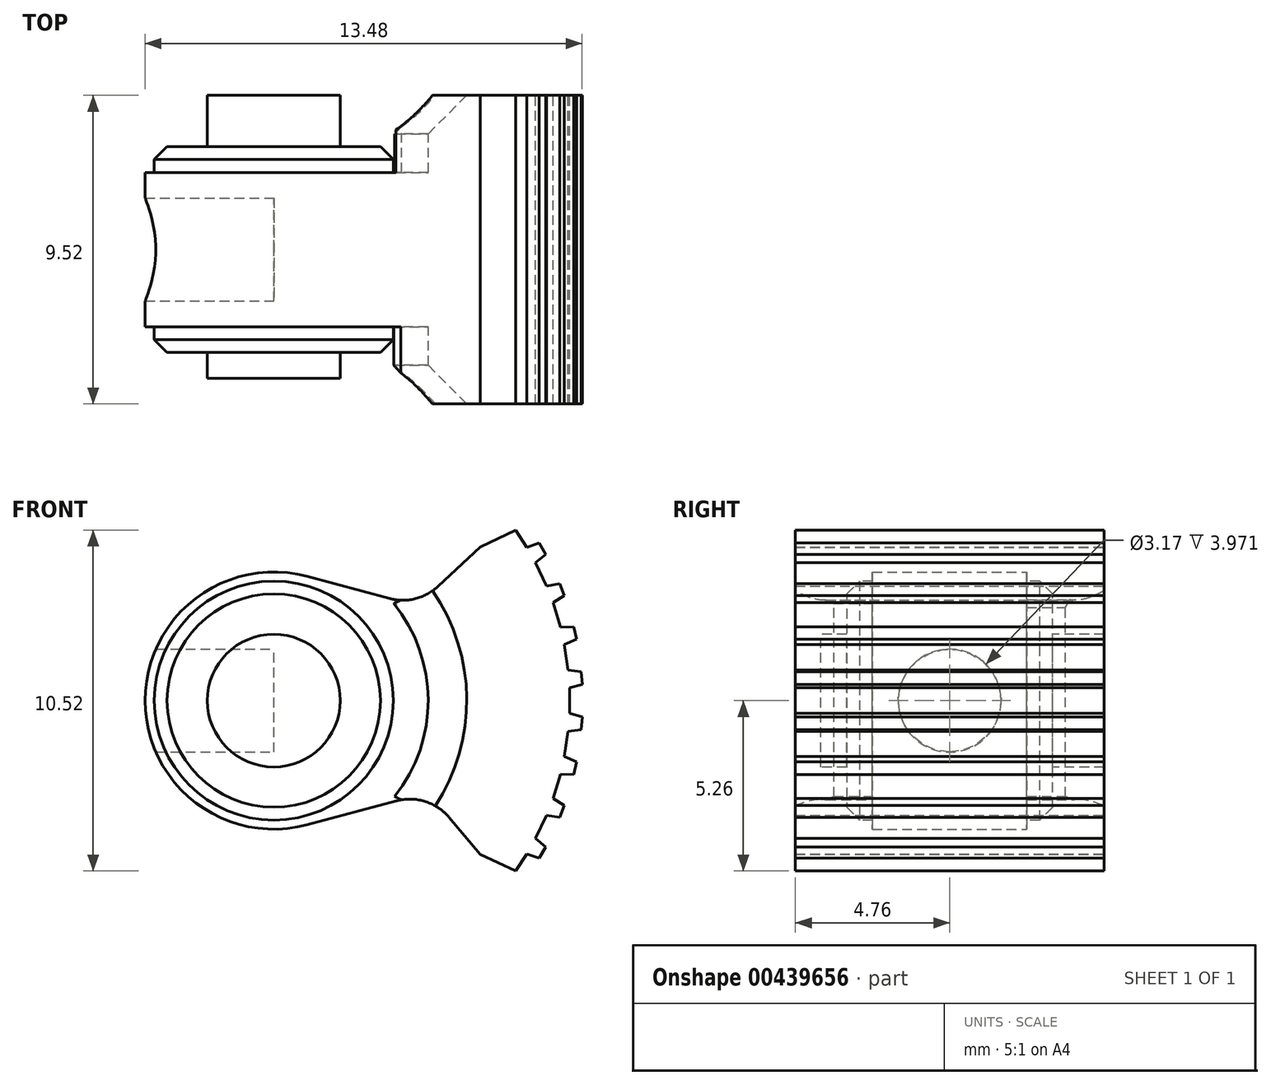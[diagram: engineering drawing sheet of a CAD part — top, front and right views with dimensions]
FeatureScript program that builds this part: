
annotation { "Feature Type Name" : "Feature", "Feature Type Description" : "" }
export const myFeature = defineFeature(function(context is Context, id is Id, definition is map)
    precondition{}
    {
        {
            var Q0;
            Q0=qCreatedBy(makeId("Front.planeOp"),FACE);
            var sketch = newSketch(context, id + "F0", { "sketchPlane" : qUnion([Q0])});
            skCircle(sketch, "E0", {"center": v(0, 0) * mm, "radius": 9.53 * mm, "construction": true});
            skCircle(sketch, "E1", {"center": v(0, 0) * mm, "radius": 7.94 * mm, "construction": true});
            skCircle(sketch, "E2", {"center": v(0, 0) * mm, "radius": 4.76 * mm, "construction": true});
            skCircle(sketch, "E3", {"center": v(0, 0) * mm, "radius": 3.97 * mm});
            skLineSegment(sketch, "E4", {"start": v(-17.92, 8.9) * mm, "end": v(15.33, 0) * mm, "construction": true});
            skLineSegment(sketch, "E5", {"start": v(-17.92, -8.9) * mm, "end": v(15.33, 0) * mm, "construction": true});
            skLineSegment(sketch, "E6", {"start": v(3.57, 3.15) * mm, "end": v(1.03, 3.83) * mm});
            skLineSegment(sketch, "E7", {"start": v(3.78, -3.1) * mm, "end": v(1.03, -3.83) * mm});
            skArc(sketch, "E8", {"start": v(4.23, -2.2) * mm, "mid": v(4.76, 0) * mm, "end": v(4.23, 2.2) * mm});
            skLineSegment(sketch, "E9", {"start": v(2.38, 0) * mm, "end": v(14.12, 14) * mm, "construction": true});
            skLineSegment(sketch, "E10", {"start": v(2.38, 0) * mm, "end": v(14.12, -14) * mm, "construction": true});
            skLineSegment(sketch, "E11", {"start": v(5.07, 3.53) * mm, "end": v(6.36, 4.75) * mm});
            skLineSegment(sketch, "E12", {"start": v(5.4, -3.6) * mm, "end": v(6.36, -4.75) * mm});
            skArc(sketch, "E13.filletArc", {"start": v(3.57, 3.15) * mm, "mid": v(4.37, 3.15) * mm, "end": v(5.07, 3.53) * mm});
            skArc(sketch, "E14.filletArc", {"start": v(5.4, -3.6) * mm, "mid": v(4.67, -3.11) * mm, "end": v(3.78, -3.1) * mm});
            skLineSegment(sketch, "E15", {"start": v(6.36, 4.75) * mm, "end": v(14.46, 8.52) * mm, "construction": true});
            skLineSegment(sketch, "E16", {"start": v(6.36, -4.75) * mm, "end": v(14.46, -8.52) * mm, "construction": true});
            skLineSegment(sketch, "E17", {"start": v(6.36, 4.75) * mm, "end": v(7.83, 5.43) * mm});
            skLineSegment(sketch, "E18", {"start": v(6.36, -4.75) * mm, "end": v(7.83, -5.43) * mm});
            skArc(sketch, "E19", {"start": v(7.83, -5.43) * mm, "mid": v(9.53, 0) * mm, "end": v(7.83, 5.43) * mm});
            skCircle(sketch, "E20", {"center": v(0, 0) * mm, "radius": 9.13 * mm, "construction": true});
            skSolve(sketch);
        }
        {
            var Q0;
            Q0=qSketchRegion(id+"F0",true);
            extrude(context, id + "F1", {"entities" : qUnion([Q0]), "endBound" : BoundingType.SYMMETRIC, "depth" : 4.76 * mm});
        }
        {
            var Q0;
            Q0=qCreatedBy(makeId("Top.planeOp"),FACE);
            var sketch = newSketch(context, id + "F2", { "sketchPlane" : qUnion([Q0])});
            skLineSegment(sketch, "E21", {"start": v(0, -3.18) * mm, "end": v(0, 3.18) * mm});
            skLineSegment(sketch, "E22", {"start": v(0, 3.18) * mm, "end": v(0, 4.76) * mm});
            skLineSegment(sketch, "E23", {"start": v(0, 4.76) * mm, "end": v(2.05, 4.76) * mm});
            skLineSegment(sketch, "E24", {"start": v(2.05, 4.76) * mm, "end": v(2.05, 3.18) * mm});
            skLineSegment(sketch, "E25", {"start": v(2.05, 3.18) * mm, "end": v(3.69, 3.18) * mm});
            skLineSegment(sketch, "E26", {"start": v(3.69, 3.18) * mm, "end": v(3.69, -3.18) * mm});
            skLineSegment(sketch, "E27", {"start": v(3.69, -3.18) * mm, "end": v(2.05, -3.18) * mm});
            skLineSegment(sketch, "E28", {"start": v(2.05, -3.18) * mm, "end": v(2.05, -3.97) * mm});
            skLineSegment(sketch, "E29", {"start": v(2.05, -3.97) * mm, "end": v(0, -3.97) * mm});
            skLineSegment(sketch, "E30", {"start": v(0, -3.97) * mm, "end": v(0, -3.18) * mm});
            skSolve(sketch);
        }
        {
            var Q0;
            Q0=makeQuery(id+"F2.imprint","IMPRINT",FACE,{"disambiguationData":[TD([[makeQuery(id+"F2.imprint","IMPRINT",EDGE,{"derivedFrom":sQuery(id+"F2.wireOp",EDGE,"E21")}),-1.0]])]});
            var Q1;
            Q1=sQuery(id+"F2.wireOp",EDGE,"E21");
            revolve(context, id + "F3", {"operationType" : NewBodyOperationType.ADD, "entities" : qUnion([Q0]), "axis" : qUnion([Q1]), "revolveType" : RevolveType.FULL});
        }
        {
            var Q0;
            Q0=qCreatedBy(makeId("Front.planeOp"),FACE);
            var sketch = newSketch(context, id + "F4", { "sketchPlane" : qUnion([Q0])});
            skArc(sketch, "E31.0", {"start": v(7.83, -5.43) * mm, "mid": v(9.53, 0) * mm, "end": v(7.83, 5.43) * mm});
            skLineSegment(sketch, "E32.0", {"start": v(6.36, 4.75) * mm, "end": v(7.83, 5.43) * mm});
            skLineSegment(sketch, "E33.0", {"start": v(5.07, 3.53) * mm, "end": v(6.36, 4.75) * mm});
            skLineSegment(sketch, "E33.1", {"start": v(5.4, -3.6) * mm, "end": v(6.36, -4.75) * mm});
            skLineSegment(sketch, "E33.2", {"start": v(6.36, -4.75) * mm, "end": v(7.83, -5.43) * mm});
            skArc(sketch, "E34.0", {"start": v(3.57, 3.15) * mm, "mid": v(4.37, 3.15) * mm, "end": v(5.07, 3.53) * mm});
            skArc(sketch, "E34.1", {"start": v(5.4, -3.6) * mm, "mid": v(4.67, -3.11) * mm, "end": v(3.78, -3.1) * mm});
            skCircle(sketch, "E35", {"center": v(0, 0) * mm, "radius": 4.76 * mm, "construction": true});
            skLineSegment(sketch, "E36.0", {"start": v(3.57, 3.15) * mm, "end": v(3.57, 3.15) * mm});
            skLineSegment(sketch, "E37.0", {"start": v(3.78, -3.1) * mm, "end": v(3.57, -3.15) * mm});
            skArc(sketch, "E38", {"start": v(3.57, -3.15) * mm, "mid": v(4.76, 0) * mm, "end": v(3.57, 3.15) * mm});
            skPoint(sketch, "E39.orphan", {"position": v(1.03, 3.83) * mm});
            skPoint(sketch, "E40.orphan", {"position": v(1.03, -3.83) * mm});
            skSolve(sketch);
        }
        {
            var Q0;
            Q0=qSketchRegion(id+"F4",true);
            extrude(context, id + "F5", {"entities" : qUnion([Q0]), "operationType" : NewBodyOperationType.ADD, "endBound" : BoundingType.SYMMETRIC, "depth" : 9.52 * mm});
        }
        {
            var Q0;
            Q0=makeQuery(id+"F3.opRevolve","SWEPT_EDGE",EDGE,{"disambiguationData":[OSD([sQuery(id+"F2.wireOp",EDGE,"E26"),sQuery(id+"F2.wireOp",EDGE,"E27")])]});
            var Q1;
            Q1=makeQuery(id+"F3.opRevolve","SWEPT_EDGE",EDGE,{"disambiguationData":[OSD([sQuery(id+"F2.wireOp",EDGE,"E25"),sQuery(id+"F2.wireOp",EDGE,"E26")])]});
            chamfer(context, id + "F6", {"entities" : qUnion([Q0, Q1]), "chamferType" : ChamferType.OFFSET_ANGLE, "width" : 0.4 * mm, "oppositeDirection" : false, "angle" : 45 * degree, "tangentPropagation" : true});
        }
        {
            var Q0;
            Q0=makeQuery(id+"F5.opExtrude","CAP_EDGE",EDGE,{"disambiguationData":[OSD([sQuery(id+"F4.wireOp",EDGE,"E38")])],"isStart":false});
            var Q1;
            Q1=makeQuery(id+"F5.opExtrude","CAP_EDGE",EDGE,{"disambiguationData":[OSD([sQuery(id+"F4.wireOp",EDGE,"E38")])],"isStart":true});
            chamfer(context, id + "F7", {"entities" : qUnion([Q0, Q1]), "chamferType" : ChamferType.OFFSET_ANGLE, "width" : 1.2 * mm, "oppositeDirection" : false, "angle" : 45 * degree, "tangentPropagation" : true});
        }
        {
            var Q0;
            {var subQ0=sQuery(id+"F4.wireOp",EDGE,"E37.0");var subQ2=sQuery(id+"F4.wireOp",EDGE,"E38");Q0=makeQuery(id+"F5.boolean.opBoolean","SPLIT",EDGE,{"disambiguationData":[TD([makeQuery(id+"F5.opExtrude","CAP_FACE",FACE,{"disambiguationData":[OSD([sQuery(id+"F4.wireOp",EDGE,"E31.0"),sQuery(id+"F4.wireOp",EDGE,"E32.0"),sQuery(id+"F4.wireOp",EDGE,"E33.0"),sQuery(id+"F4.wireOp",EDGE,"E33.1"),sQuery(id+"F4.wireOp",EDGE,"E33.2"),sQuery(id+"F4.wireOp",EDGE,"E34.0"),sQuery(id+"F4.wireOp",EDGE,"E34.1"),subQ0,subQ2])],"isStart":false})])],"derivedFrom":makeQuery(id+"F5.opExtrude","SWEPT_EDGE",EDGE,{"disambiguationData":[OSD([subQ0,subQ2])]})});}
            var Q1;
            {var subQ0=sQuery(id+"F4.wireOp",EDGE,"E37.0");var subQ1=sQuery(id+"F4.wireOp",EDGE,"E38");Q1=makeQuery(id+"F5.boolean.opBoolean","SPLIT",EDGE,{"disambiguationData":[TD([makeQuery(id+"F5.opExtrude","CAP_FACE",FACE,{"disambiguationData":[OSD([sQuery(id+"F4.wireOp",EDGE,"E31.0"),sQuery(id+"F4.wireOp",EDGE,"E32.0"),sQuery(id+"F4.wireOp",EDGE,"E33.0"),sQuery(id+"F4.wireOp",EDGE,"E33.1"),sQuery(id+"F4.wireOp",EDGE,"E33.2"),sQuery(id+"F4.wireOp",EDGE,"E34.0"),sQuery(id+"F4.wireOp",EDGE,"E34.1"),subQ0,subQ1])],"isStart":true})])],"derivedFrom":makeQuery(id+"F5.opExtrude","SWEPT_EDGE",EDGE,{"disambiguationData":[OSD([subQ0,subQ1])]})});}
            var Q2;
            {var subQ1=sQuery(id+"F4.wireOp",EDGE,"E38");var subQ2=sQuery(id+"F4.wireOp",EDGE,"E34.0");Q2=makeQuery(id+"F5.boolean.opBoolean","SPLIT",EDGE,{"disambiguationData":[TD([makeQuery(id+"F5.opExtrude","CAP_FACE",FACE,{"disambiguationData":[OSD([sQuery(id+"F4.wireOp",EDGE,"E31.0"),sQuery(id+"F4.wireOp",EDGE,"E32.0"),sQuery(id+"F4.wireOp",EDGE,"E33.0"),sQuery(id+"F4.wireOp",EDGE,"E33.1"),sQuery(id+"F4.wireOp",EDGE,"E33.2"),subQ2,sQuery(id+"F4.wireOp",EDGE,"E34.1"),sQuery(id+"F4.wireOp",EDGE,"E37.0"),subQ1])],"isStart":false})])],"derivedFrom":makeQuery(id+"F5.opExtrude","SWEPT_EDGE",EDGE,{"disambiguationData":[OSD([subQ2,subQ1])]})});}
            var Q3;
            {var subQ0=sQuery(id+"F4.wireOp",EDGE,"E38");var subQ1=sQuery(id+"F4.wireOp",EDGE,"E34.0");Q3=makeQuery(id+"F5.boolean.opBoolean","SPLIT",EDGE,{"disambiguationData":[TD([makeQuery(id+"F5.opExtrude","CAP_FACE",FACE,{"disambiguationData":[OSD([sQuery(id+"F4.wireOp",EDGE,"E31.0"),sQuery(id+"F4.wireOp",EDGE,"E32.0"),sQuery(id+"F4.wireOp",EDGE,"E33.0"),sQuery(id+"F4.wireOp",EDGE,"E33.1"),sQuery(id+"F4.wireOp",EDGE,"E33.2"),subQ1,sQuery(id+"F4.wireOp",EDGE,"E34.1"),sQuery(id+"F4.wireOp",EDGE,"E37.0"),subQ0])],"isStart":true})])],"derivedFrom":makeQuery(id+"F5.opExtrude","SWEPT_EDGE",EDGE,{"disambiguationData":[OSD([subQ1,subQ0])]})});}
            chamfer(context, id + "F8", {"entities" : qUnion([Q0, Q1, Q2, Q3]), "chamferType" : ChamferType.OFFSET_ANGLE, "width" : 0.4 * mm, "oppositeDirection" : false, "angle" : 45 * degree, "tangentPropagation" : true});
        }
        {
            var Q0;
            Q0=makeQuery(id+"F5.opExtrude","CAP_FACE",FACE,{"disambiguationData":[OSD([sQuery(id+"F4.wireOp",EDGE,"E31.0"),sQuery(id+"F4.wireOp",EDGE,"E32.0"),sQuery(id+"F4.wireOp",EDGE,"E33.0"),sQuery(id+"F4.wireOp",EDGE,"E33.1"),sQuery(id+"F4.wireOp",EDGE,"E33.2"),sQuery(id+"F4.wireOp",EDGE,"E34.0"),sQuery(id+"F4.wireOp",EDGE,"E34.1"),sQuery(id+"F4.wireOp",EDGE,"E37.0"),sQuery(id+"F4.wireOp",EDGE,"E38")])],"isStart":true});
            var sketch = newSketch(context, id + "F9", { "sketchPlane" : qUnion([Q0])});
            skArc(sketch, "E41.0", {"start": v(-7.83, -5.43) * mm, "mid": v(-9.53, 0) * mm, "end": v(-7.83, 5.43) * mm, "construction": true});
            skCircle(sketch, "E42", {"center": v(0, 0) * mm, "radius": 9.13 * mm, "construction": true});
            skCircle(sketch, "E43", {"center": v(0, 0) * mm, "radius": 7.64 * mm, "construction": true});
            skCircle(sketch, "E44", {"center": v(0, 0) * mm, "radius": 9.53 * mm, "construction": true});
            skLineSegment(sketch, "E45", {"start": v(-7.64, 0) * mm, "end": v(-9.51, -0.5) * mm, "construction": true});
            skLineSegment(sketch, "E46", {"start": v(-7.64, 0) * mm, "end": v(-9.51, 0.5) * mm, "construction": true});
            skLineSegment(sketch, "E47", {"start": v(-9.12, 0.4) * mm, "end": v(-9.12, -0.4) * mm});
            skLineSegment(sketch, "E48", {"start": v(-9.51, 0.5) * mm, "end": v(-9.48, 0.9) * mm});
            skLineSegment(sketch, "E49", {"start": v(-9.51, 0.5) * mm, "end": v(-9.12, 0.4) * mm});
            skLineSegment(sketch, "E50", {"start": v(-9.12, -0.4) * mm, "end": v(-9.51, -0.5) * mm});
            skLineSegment(sketch, "E51", {"start": v(-9.51, -0.5) * mm, "end": v(-9.48, -0.9) * mm, "construction": true});
            skLineSegment(sketch, "E52", {"start": v(-9.48, -0.9) * mm, "end": v(-7.56, -1.12) * mm, "construction": true});
            skLineSegment(sketch, "E53", {"start": v(-7.56, -1.12) * mm, "end": v(-9.34, -1.9) * mm, "construction": true});
            skLineSegment(sketch, "E54", {"start": v(-9.34, -1.9) * mm, "end": v(-9.25, -2.28) * mm, "construction": true});
            skLineSegment(sketch, "E55", {"start": v(-9.25, -2.28) * mm, "end": v(-7.31, -2.22) * mm, "construction": true});
            skLineSegment(sketch, "E56", {"start": v(-7.31, -2.22) * mm, "end": v(-8.96, -3.24) * mm, "construction": true});
            skLineSegment(sketch, "E57", {"start": v(-8.96, -3.24) * mm, "end": v(-8.81, -3.6) * mm, "construction": true});
            skLineSegment(sketch, "E58", {"start": v(-8.81, -3.6) * mm, "end": v(-6.9, -3.26) * mm, "construction": true});
            skLineSegment(sketch, "E59", {"start": v(-6.9, -3.26) * mm, "end": v(-8.39, -4.52) * mm, "construction": true});
            skLineSegment(sketch, "E60", {"start": v(-8.39, -4.52) * mm, "end": v(-8.2, -4.86) * mm, "construction": true});
            skLineSegment(sketch, "E61", {"start": v(-8.2, -4.86) * mm, "end": v(-6.35, -4.24) * mm, "construction": true});
            skLineSegment(sketch, "E62", {"start": v(-6.35, -4.24) * mm, "end": v(-7.63, -5.7) * mm, "construction": true});
            skLineSegment(sketch, "E63", {"start": v(-10.21, 0) * mm, "end": v(-9.13, 0) * mm});
            skLineSegment(sketch, "E64", {"start": v(-9.13, 0) * mm, "end": v(-9.12, -0.4) * mm});
            skLineSegment(sketch, "E65", {"start": v(-9.51, -0.5) * mm, "end": v(-9.48, -0.9) * mm});
            skLineSegment(sketch, "E66", {"start": v(-9.48, -0.9) * mm, "end": v(-9.08, -0.94) * mm});
            skLineSegment(sketch, "E67", {"start": v(-9.08, -0.94) * mm, "end": v(-8.96, -1.73) * mm});
            skLineSegment(sketch, "E68", {"start": v(-8.96, -1.73) * mm, "end": v(-9.34, -1.9) * mm});
            skLineSegment(sketch, "E69", {"start": v(-9.34, -1.9) * mm, "end": v(-9.25, -2.28) * mm});
            skLineSegment(sketch, "E70", {"start": v(-9.25, -2.28) * mm, "end": v(-8.84, -2.26) * mm});
            skLineSegment(sketch, "E71", {"start": v(-8.61, -3.02) * mm, "end": v(-8.84, -2.26) * mm});
            skLineSegment(sketch, "E72", {"start": v(-8.61, -3.02) * mm, "end": v(-8.96, -3.24) * mm});
            skLineSegment(sketch, "E73", {"start": v(-8.96, -3.24) * mm, "end": v(-8.81, -3.6) * mm});
            skLineSegment(sketch, "E74", {"start": v(-8.81, -3.6) * mm, "end": v(-8.42, -3.54) * mm});
            skLineSegment(sketch, "E75", {"start": v(-8.42, -3.54) * mm, "end": v(-8.08, -4.25) * mm});
            skLineSegment(sketch, "E76", {"start": v(-8.08, -4.25) * mm, "end": v(-8.39, -4.52) * mm});
            skLineSegment(sketch, "E77", {"start": v(-8.39, -4.52) * mm, "end": v(-8.2, -4.86) * mm});
            skLineSegment(sketch, "E78", {"start": v(-8.2, -4.86) * mm, "end": v(-7.8, -4.73) * mm});
            skLineSegment(sketch, "E79", {"start": v(-7.8, -4.73) * mm, "end": v(-7.37, -5.4) * mm});
            skLineSegment(sketch, "E80", {"start": v(-7.37, -5.4) * mm, "end": v(-8.24, -6.4) * mm});
            skLineSegment(sketch, "E81", {"start": v(-8.24, -6.4) * mm, "end": v(-10.21, 0) * mm});
            skLineSegment(sketch, "E82.MirrorCS", {"start": v(-8.24, 6.4) * mm, "end": v(-10.21, 0) * mm});
            skLineSegment(sketch, "E83.MirrorCS", {"start": v(-9.12, -0.4) * mm, "end": v(-9.12, 0.4) * mm});
            skLineSegment(sketch, "E84.MirrorCS", {"start": v(-9.12, 0.4) * mm, "end": v(-9.51, 0.5) * mm});
            skLineSegment(sketch, "E85.MirrorCS", {"start": v(-9.48, 0.9) * mm, "end": v(-9.08, 0.94) * mm});
            skLineSegment(sketch, "E86.MirrorCS", {"start": v(-9.08, 0.94) * mm, "end": v(-8.96, 1.73) * mm});
            skLineSegment(sketch, "E87.MirrorCS", {"start": v(-8.96, 1.73) * mm, "end": v(-9.34, 1.9) * mm});
            skLineSegment(sketch, "E88.MirrorCS", {"start": v(-9.34, 1.9) * mm, "end": v(-9.25, 2.28) * mm});
            skLineSegment(sketch, "E89.MirrorCS", {"start": v(-9.25, 2.28) * mm, "end": v(-8.84, 2.26) * mm});
            skLineSegment(sketch, "E90.MirrorCS", {"start": v(-8.61, 3.02) * mm, "end": v(-8.84, 2.26) * mm});
            skLineSegment(sketch, "E91.MirrorCS", {"start": v(-8.61, 3.02) * mm, "end": v(-8.96, 3.24) * mm});
            skLineSegment(sketch, "E92.MirrorCS", {"start": v(-8.96, 3.24) * mm, "end": v(-8.81, 3.6) * mm});
            skLineSegment(sketch, "E93.MirrorCS", {"start": v(-8.81, 3.6) * mm, "end": v(-8.42, 3.54) * mm});
            skLineSegment(sketch, "E94.MirrorCS", {"start": v(-8.42, 3.54) * mm, "end": v(-8.08, 4.25) * mm});
            skLineSegment(sketch, "E95.MirrorCS", {"start": v(-8.08, 4.25) * mm, "end": v(-8.39, 4.52) * mm});
            skLineSegment(sketch, "E96.MirrorCS", {"start": v(-8.39, 4.52) * mm, "end": v(-8.2, 4.86) * mm});
            skLineSegment(sketch, "E97.MirrorCS", {"start": v(-8.2, 4.86) * mm, "end": v(-7.8, 4.73) * mm});
            skLineSegment(sketch, "E98.MirrorCS", {"start": v(-7.8, 4.73) * mm, "end": v(-7.37, 5.4) * mm});
            skLineSegment(sketch, "E99.MirrorCS", {"start": v(-7.37, 5.4) * mm, "end": v(-8.24, 6.4) * mm});
            skSolve(sketch);
        }
        {
            var Q0;
            Q0=qSketchRegion(id+"F9",true);
            var Q1;
            Q1=makeQuery(id+"F5.opExtrude","CAP_FACE",FACE,{"disambiguationData":[OSD([sQuery(id+"F4.wireOp",EDGE,"E31.0"),sQuery(id+"F4.wireOp",EDGE,"E32.0"),sQuery(id+"F4.wireOp",EDGE,"E33.0"),sQuery(id+"F4.wireOp",EDGE,"E33.1"),sQuery(id+"F4.wireOp",EDGE,"E33.2"),sQuery(id+"F4.wireOp",EDGE,"E34.0"),sQuery(id+"F4.wireOp",EDGE,"E34.1"),sQuery(id+"F4.wireOp",EDGE,"E37.0"),sQuery(id+"F4.wireOp",EDGE,"E38")])],"isStart":false});
            extrude(context, id + "F10", {"entities" : qUnion([Q0]), "operationType" : NewBodyOperationType.REMOVE, "endBound" : BoundingType.UP_TO_SURFACE, "oppositeDirection" : true, "endBoundEntityFace" : qUnion([Q1]), "depth" : 25.4 * mm});
        }
        {
            var Q0;
            Q0=qCreatedBy(makeId("Right.planeOp"),FACE);
            var sketch = newSketch(context, id + "F11", { "sketchPlane" : qUnion([Q0])});
            skCircle(sketch, "E100", {"center": v(0, 0) * mm, "radius": 1.59 * mm});
            skSolve(sketch);
        }
        {
            var Q0;
            Q0=qSketchRegion(id+"F11",true);
            extrude(context, id + "F12", {"entities" : qUnion([Q0]), "operationType" : NewBodyOperationType.REMOVE, "endBound" : BoundingType.UP_TO_NEXT, "oppositeDirection" : true, "depth" : 25.4 * mm});
        }
    });
